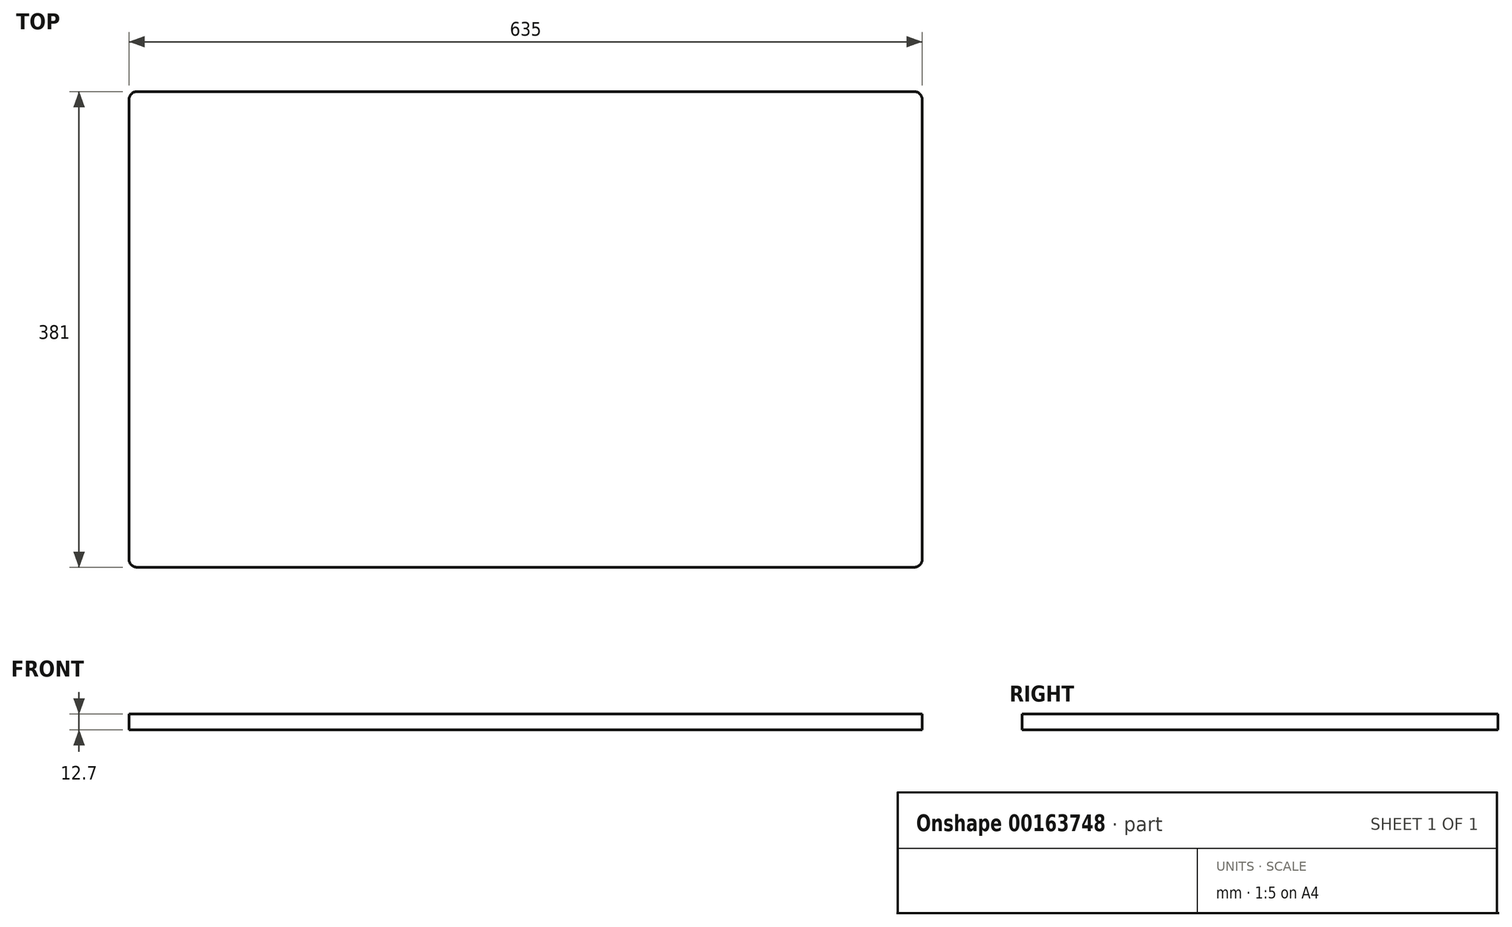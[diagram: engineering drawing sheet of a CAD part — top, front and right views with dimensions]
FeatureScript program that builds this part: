
annotation { "Feature Type Name" : "Feature", "Feature Type Description" : "" }
export const myFeature = defineFeature(function(context is Context, id is Id, definition is map)
    precondition{}
    {
        {
            var Q0;
            Q0=qCreatedBy(makeId("Top.planeOp"),FACE);
            var sketch = newSketch(context, id + "F0", { "sketchPlane" : qUnion([Q0])});
            skLineSegment(sketch, "E0.bottom", {"start": v(-311.15, 190.5) * mm, "end": v(311.15, 190.5) * mm});
            skLineSegment(sketch, "E0.top", {"start": v(-311.15, -190.5) * mm, "end": v(311.15, -190.5) * mm});
            skLineSegment(sketch, "E0.left", {"start": v(-317.5, 184.15) * mm, "end": v(-317.5, -184.15) * mm});
            skLineSegment(sketch, "E0.right", {"start": v(317.5, 184.15) * mm, "end": v(317.5, -184.15) * mm});
            skPoint(sketch, "E0.middle", {"position": v(0, 0) * mm});
            skPoint(sketch, "E1.visualSharp", {"position": v(-317.5, 190.5) * mm});
            skArc(sketch, "E1.filletArc", {"start": v(-311.15, 190.5) * mm, "mid": v(-315.64, 188.64) * mm, "end": v(-317.5, 184.15) * mm});
            skPoint(sketch, "E2.visualSharp", {"position": v(317.5, 190.5) * mm});
            skArc(sketch, "E2.filletArc", {"start": v(317.5, 184.15) * mm, "mid": v(315.64, 188.64) * mm, "end": v(311.15, 190.5) * mm});
            skPoint(sketch, "E3.visualSharp", {"position": v(317.5, -190.5) * mm});
            skArc(sketch, "E3.filletArc", {"start": v(311.15, -190.5) * mm, "mid": v(315.64, -188.64) * mm, "end": v(317.5, -184.15) * mm});
            skPoint(sketch, "E4.visualSharp", {"position": v(-317.5, -190.5) * mm});
            skArc(sketch, "E4.filletArc", {"start": v(-317.5, -184.15) * mm, "mid": v(-315.64, -188.64) * mm, "end": v(-311.15, -190.5) * mm});
            skSolve(sketch);
        }
        {
            var Q0;
            Q0=qSketchRegion(id+"F0",true);
            extrude(context, id + "F1", {"entities" : qUnion([Q0]), "depth" : 12.7 * mm});
        }
    });
